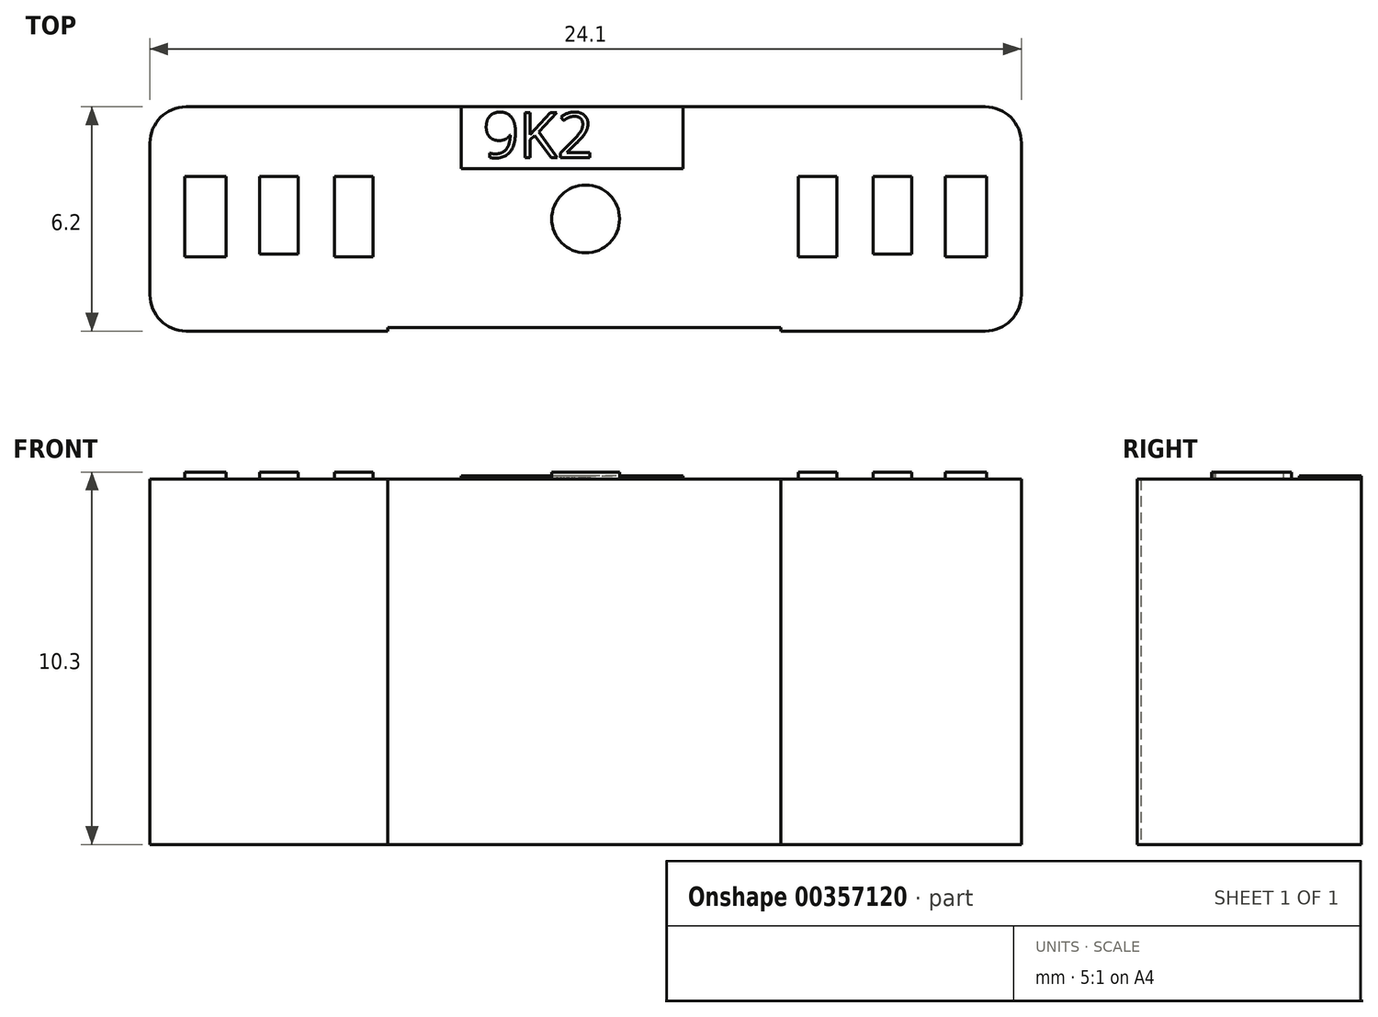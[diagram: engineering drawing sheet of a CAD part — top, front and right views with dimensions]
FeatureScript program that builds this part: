
annotation { "Feature Type Name" : "Feature", "Feature Type Description" : "" }
export const myFeature = defineFeature(function(context is Context, id is Id, definition is map)
    precondition{}
    {
        {
            var Q0;
            Q0=qCreatedBy(makeId("Front.planeOp"),FACE);
            var sketch = newSketch(context, id + "F0", { "sketchPlane" : qUnion([Q0])});
            skLineSegment(sketch, "E0.bottom", {"start": v(12.05, 5.05) * mm, "end": v(-12.05, 5.05) * mm});
            skLineSegment(sketch, "E0.top", {"start": v(12.05, -5.05) * mm, "end": v(-12.05, -5.05) * mm});
            skLineSegment(sketch, "E0.left", {"start": v(12.05, 5.05) * mm, "end": v(12.05, -5.05) * mm});
            skLineSegment(sketch, "E0.right", {"start": v(-12.05, 5.05) * mm, "end": v(-12.05, -5.05) * mm});
            skPoint(sketch, "E0.middle", {"position": v(0, 0) * mm});
            skSolve(sketch);
        }
        {
            var Q0;
            Q0 = qSketchRegion(id + "F0", true);
            extrude(context, id + "F1", {"entities" : qUnion([Q0]), "endBound" : BoundingType.SYMMETRIC, "depth" : 6.2 * mm});
        }
        {
            var Q0;
            Q0=makeQuery(id+"F1.opExtrude","SWEPT_FACE",FACE,{"disambiguationData":[OSD([sQuery(id+"F0.wireOp",EDGE,"E0.bottom")])]});
            var sketch = newSketch(context, id + "F2", { "sketchPlane" : qUnion([Q0])});
            skLineSegment(sketch, "E1", {"start": v(-11.1, 1.17) * mm, "end": v(-11.1, -1.04) * mm});
            skLineSegment(sketch, "E2", {"start": v(-11.1, -1.04) * mm, "end": v(-9.95, -1.04) * mm});
            skLineSegment(sketch, "E3", {"start": v(-9.95, -1.04) * mm, "end": v(-9.95, 1.17) * mm});
            skLineSegment(sketch, "E4", {"start": v(-11.1, 1.17) * mm, "end": v(-9.95, 1.17) * mm});
            skLineSegment(sketch, "E5", {"start": v(-9.02, 1.17) * mm, "end": v(-9.02, -0.97) * mm});
            skLineSegment(sketch, "E6", {"start": v(-9.02, -0.97) * mm, "end": v(-7.95, -0.97) * mm});
            skLineSegment(sketch, "E7", {"start": v(-7.95, -0.97) * mm, "end": v(-7.95, 1.17) * mm});
            skLineSegment(sketch, "E8", {"start": v(-7.95, 1.17) * mm, "end": v(-9.02, 1.17) * mm});
            skLineSegment(sketch, "E9", {"start": v(-6.95, 1.17) * mm, "end": v(-6.95, -1.04) * mm});
            skLineSegment(sketch, "E10", {"start": v(-6.95, -1.04) * mm, "end": v(-5.88, -1.04) * mm});
            skLineSegment(sketch, "E11", {"start": v(-5.88, -1.04) * mm, "end": v(-5.88, 1.17) * mm});
            skLineSegment(sketch, "E12", {"start": v(-6.95, 1.17) * mm, "end": v(-5.88, 1.17) * mm});
            skLineSegment(sketch, "E13.MirrorCS", {"start": v(5.88, -1.04) * mm, "end": v(5.88, 1.17) * mm});
            skLineSegment(sketch, "E14.MirrorCS", {"start": v(6.95, 1.17) * mm, "end": v(6.95, -1.04) * mm});
            skLineSegment(sketch, "E15.MirrorCS", {"start": v(9.02, 1.17) * mm, "end": v(9.02, -0.97) * mm});
            skLineSegment(sketch, "E16.MirrorCS", {"start": v(7.95, -0.97) * mm, "end": v(7.95, 1.17) * mm});
            skLineSegment(sketch, "E17.MirrorCS", {"start": v(9.95, -1.04) * mm, "end": v(9.95, 1.17) * mm});
            skLineSegment(sketch, "E18.MirrorCS", {"start": v(11.1, 1.17) * mm, "end": v(11.1, -1.04) * mm});
            skLineSegment(sketch, "E19", {"start": v(5.88, 1.17) * mm, "end": v(6.95, 1.17) * mm});
            skLineSegment(sketch, "E20", {"start": v(5.88, -1.04) * mm, "end": v(6.95, -1.04) * mm});
            skLineSegment(sketch, "E21", {"start": v(7.95, 1.17) * mm, "end": v(9.02, 1.17) * mm});
            skLineSegment(sketch, "E22", {"start": v(7.95, -0.97) * mm, "end": v(9.02, -0.97) * mm});
            skLineSegment(sketch, "E23", {"start": v(9.95, 1.17) * mm, "end": v(11.1, 1.17) * mm});
            skLineSegment(sketch, "E24", {"start": v(9.95, -1.04) * mm, "end": v(11.1, -1.04) * mm});
            skCircle(sketch, "E25", {"center": v(0, 0) * mm, "radius": 0.94 * mm});
            skSolve(sketch);
        }
        {
            var Q0;
            Q0 = qSketchRegion(id + "F2", true);
            extrude(context, id + "F3", {"entities" : qUnion([Q0]), "operationType" : NewBodyOperationType.ADD, "depth" : .2 * mm});
        }
        {
            var Q0;
            Q0=makeQuery(id+"F1.opExtrude","CAP_EDGE",EDGE,{"disambiguationData":[OSD([sQuery(id+"F0.wireOp",EDGE,"E0.right")])],"isStart":true});
            fillet(context, id + "F4", {"entities" : qUnion([Q0]), "radius" : 1 * mm, "tangentPropagation" : true, "allowEdgeOverflow" : false});
        }
        {
            var Q0;
            Q0=makeQuery(id+"F1.opExtrude","CAP_EDGE",EDGE,{"disambiguationData":[OSD([sQuery(id+"F0.wireOp",EDGE,"E0.right")])],"isStart":false});
            fillet(context, id + "F5", {"entities" : qUnion([Q0]), "radius" : 1 * mm, "tangentPropagation" : true, "allowEdgeOverflow" : false});
        }
        {
            var Q0;
            Q0=makeQuery(id+"F1.opExtrude","CAP_EDGE",EDGE,{"disambiguationData":[OSD([sQuery(id+"F0.wireOp",EDGE,"E0.left")])],"isStart":true});
            fillet(context, id + "F6", {"entities" : qUnion([Q0]), "radius" : 1 * mm, "tangentPropagation" : true, "allowEdgeOverflow" : false});
        }
        {
            var Q0;
            Q0=makeQuery(id+"F1.opExtrude","CAP_EDGE",EDGE,{"disambiguationData":[OSD([sQuery(id+"F0.wireOp",EDGE,"E0.left")])],"isStart":false});
            fillet(context, id + "F7", {"entities" : qUnion([Q0]), "radius" : 1 * mm, "tangentPropagation" : true, "allowEdgeOverflow" : false});
        }
        {
            var Q0;
            Q0=makeQuery(id+"F1.opExtrude","CAP_FACE",FACE,{"disambiguationData":[OSD([sQuery(id+"F0.wireOp",EDGE,"E0.bottom"),sQuery(id+"F0.wireOp",EDGE,"E0.top"),sQuery(id+"F0.wireOp",EDGE,"E0.left"),sQuery(id+"F0.wireOp",EDGE,"E0.right")])],"isStart":false});
            var sketch = newSketch(context, id + "F8", { "sketchPlane" : qUnion([Q0])});
            skLineSegment(sketch, "E26", {"start": v(5.4, 5.05) * mm, "end": v(5.4, -5.05) * mm});
            skLineSegment(sketch, "E27", {"start": v(-5.47, 5.05) * mm, "end": v(-5.47, -5.05) * mm});
            skLineSegment(sketch, "E28", {"start": v(-5.47, -5.05) * mm, "end": v(5.4, -5.05) * mm});
            skLineSegment(sketch, "E29", {"start": v(-5.47, 5.05) * mm, "end": v(5.4, 5.05) * mm});
            skSolve(sketch);
        }
        {
            var Q0;
            Q0 = qSketchRegion(id + "F8", true);
            extrude(context, id + "F9", {"entities" : qUnion([Q0]), "operationType" : NewBodyOperationType.REMOVE, "oppositeDirection" : true, "depth" : .1 * mm});
        }
        {
            var Q0;
            Q0=makeQuery(id+"F1.opExtrude","SWEPT_FACE",FACE,{"disambiguationData":[OSD([sQuery(id+"F0.wireOp",EDGE,"E0.bottom")])]});
            var sketch = newSketch(context, id + "F10", { "sketchPlane" : qUnion([Q0])});
            skLineSegment(sketch, "E30", {"start": v(-3.43, 3.1) * mm, "end": v(-3.43, 1.4) * mm});
            skLineSegment(sketch, "E31", {"start": v(-3.43, 1.4) * mm, "end": v(2.7, 1.4) * mm});
            skLineSegment(sketch, "E32", {"start": v(2.7, 1.38) * mm, "end": v(2.7, 3.1) * mm});
            skLineSegment(sketch, "E33", {"start": v(2.7, 3.1) * mm, "end": v(-3.43, 3.1) * mm});
            skText(sketch, "E34", { "text": "9K2", "fontName": "OpenSans-Regular.ttf"});
            const initialGuessF10  = {"E34": [-0.00284, 0.0017, 1, 0, 0.00125]};
            skSetInitialGuess(sketch, initialGuessF10);
            skSolve(sketch);
        }
        {
            var Q0;
            Q0 = qSketchRegion(id + "F10", true);
            extrude(context, id + "F11", {"entities" : qUnion([Q0]), "operationType" : NewBodyOperationType.ADD, "depth" : .1 * mm});
        }
    });
